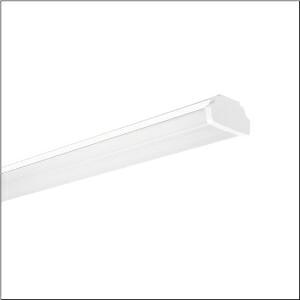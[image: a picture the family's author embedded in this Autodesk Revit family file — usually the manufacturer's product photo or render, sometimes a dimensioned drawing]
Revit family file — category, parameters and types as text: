
# Revit family: modario_r__31_gen_2_53bm8127v485c2_f877
name_source: partatom
category: Lighting Fixtures
units: mm (PartAtom-declared; Revit-internal decimal feet)

## family parameters
Cut with Voids When Loaded = No
Host = Face
Light Source = No
Part Type = Normal
Room Calculation Point = No
Round Connector Dimension = Use Diameter
Shared = No

## types (1)
- Modario® 31 Gen.2 (1 x LED, 8590 lm, 47.9 W, 4000K)
    Apparent Load = 48 VA
    CIE Flux Codes = 47 80 95 93 100
    Color Rendering = 80
    Color Temperature = 4000K
    Default Elevation = 1800 mm
    Description = Modario® 31 Gen.2, luminaire insert, of sheet steel, coil coated, white, length: 1.495mm, width: 81mm, height: 82mm, 5x system unit, system units: 299mm, LED rated luminous flux: 8.590lm, light colour: 840, control gear: ON/OFF, control gear: ECG, with plug, 3-pole, with phase selection, mains connection: 220..240V, AC, 50/60Hz, rated input power: 48W, through-wiring accessed according to module size, primary optical cover: cover, of PMMA, light emission: direct distribution, primary light characteristic: symmetric, protection rating (complete): IP20, protection rating (LED compartment): IP50, insulation class (complete): insulation class I (protective earthing), certification: CE, ENEC, VDE, UKCA, impact resistance: IK03, permissible ambient temperature for indoor applications: -35..+45°C, corresponds to IFS (International Featured Standards) requirements for safety and quality in the food industry, reducing of maximum allowable ambient temperature of 5°C with ceiling mounting, IP40 when using the optional accessory 5TP9018, packaging unit: 1 piece
    Height = 92 mm
    Lamp = 1 x LED
    Lamp Light Flux = 8590 lm
    Lamp Power = 47.9 W
    Lamp count = 1
    Length = 1495 mm
    Luminous efficacy = 179 lm/W
    Manufacturer = Siteco
    ModVariant = No
    Model = 53BM8127V485C2
    Mounting Place = Ceiling
    Mounting Type = Pendant
    Number of Poles = 1
    OnlyDefault = Yes
    Power Factor = 1
    Product Name = Modario® 31 Gen.2
    Product group = luminaire insert
    ProductGroupID = 901
    Protection Class = Protection class I
    Protection Degree = IP 20
    RLX_Detail_Level = 1
    RLX_Emergency_Light_Flux = 0 lm
    RLX_Emergency_Type = 0
    RLX_Emergency_Type_DB = No
    RlxData = <blob elided: 38741 chars, md5=9b6202f2>
    Socket = socket
    Standby Power = 0 W
    System Light Flux = 8590 lm
    System Power = 48 W
    Type Comments = Product without accessories
    Type Image = l_1319597.jpg
    URL = http://relux.com
    VarID = ---
    Voltage = 0 V
    Weight = 0.00 kg
    Width = 81 mm

## geometry (parser evidence)
native form markers: Blend x4, Sweep x11
no freeform markers — native parametric forms only
